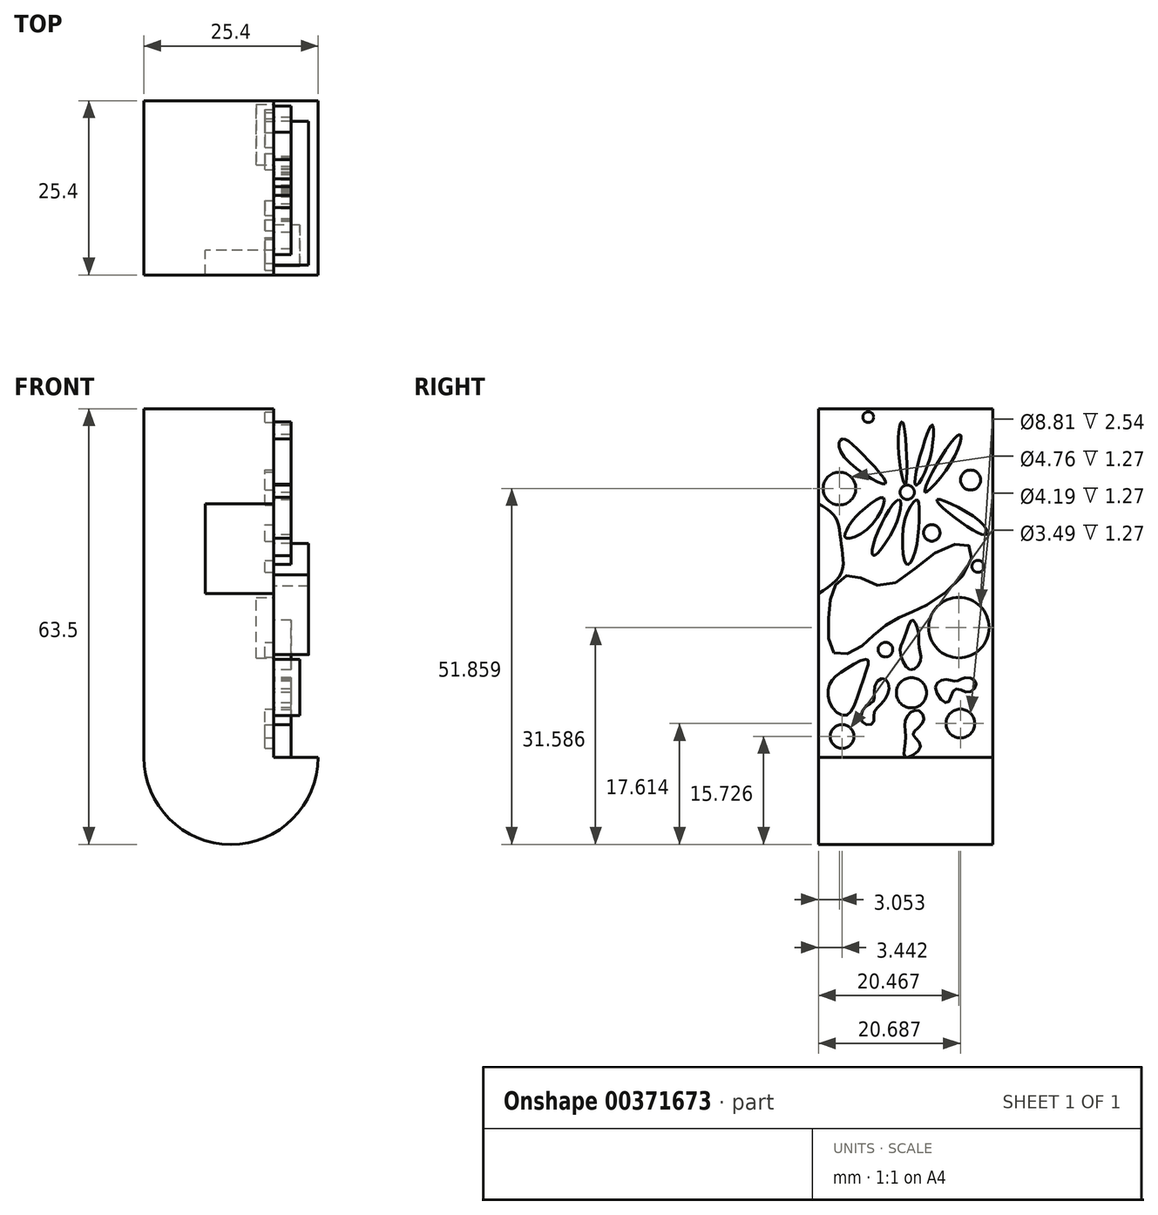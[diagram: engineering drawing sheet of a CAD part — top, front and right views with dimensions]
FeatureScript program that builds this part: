
annotation { "Feature Type Name" : "Feature", "Feature Type Description" : "" }
export const myFeature = defineFeature(function(context is Context, id is Id, definition is map)
    precondition{}
    {
        {
            var Q0;
            Q0=qCreatedBy(makeId("Front.planeOp"),FACE);
            var sketch = newSketch(context, id + "F0", { "sketchPlane" : qUnion([Q0])});
            skLineSegment(sketch, "E0.bottom", {"start": v(0, 0) * mm, "end": v(25.4, 0) * mm});
            skLineSegment(sketch, "E0.top", {"start": v(0, 50.8) * mm, "end": v(25.4, 50.8) * mm});
            skLineSegment(sketch, "E0.left", {"start": v(0, 0) * mm, "end": v(0, 50.8) * mm});
            skArc(sketch, "E1", {"start": v(0, 50.8) * mm, "mid": v(12.7, 63.5) * mm, "end": v(25.4, 50.8) * mm});
            skArc(sketch, "E2", {"start": v(0, 0) * mm, "mid": v(12.7, -12.7) * mm, "end": v(25.4, 0) * mm});
            skLineSegment(sketch, "E3", {"start": v(18.95, 50.8) * mm, "end": v(18.95, 0) * mm});
            skSolve(sketch);
        }
        {
            var Q0;
            {var subQ0=sQuery(id+"F0.wireOp",EDGE,"E0.left");Q0=makeQuery(id+"F0.imprint","IMPRINT",FACE,{"disambiguationData":[TD([[makeQuery(id+"F0.imprint","IMPRINT",EDGE,{"derivedFrom":subQ0}),-1.0]])]});}
            var Q1;
            {var subQ0=sQuery(id+"F0.wireOp",EDGE,"E1");Q1=makeQuery(id+"F0.imprint","IMPRINT",FACE,{"disambiguationData":[TD([[makeQuery(id+"F0.imprint","IMPRINT",EDGE,{"derivedFrom":subQ0}),-1.0]])]});}
            var Q2;
            {var subQ0=sQuery(id+"F0.wireOp",EDGE,"E2");Q2=makeQuery(id+"F0.imprint","IMPRINT",FACE,{"disambiguationData":[TD([[makeQuery(id+"F0.imprint","IMPRINT",EDGE,{"derivedFrom":subQ0}),1.0]])]});}
            extrude(context, id + "F1", {"entities" : qUnion([Q0, Q1, Q2]), "depth" : 25.4 * mm});
        }
        {
            var Q0;
            Q0=makeQuery(id+"F1.opExtrude","SWEPT_FACE",FACE,{"disambiguationData":[OSD([sQuery(id+"F0.wireOp",EDGE,"E3")])]});
            var sketch = newSketch(context, id + "F2", { "sketchPlane" : qUnion([Q0])});
            skPoint(sketch, "E4.5.internal.snap0", {"position": v(-12.7, 0) * mm});
            skPoint(sketch, "E4.6.internal.snap0", {"position": v(-12.7, 0) * mm});
            skFitSpline(sketch, "E4", {"points": [v(-12.7, 0) * mm, v(-10.52, 1.6) * mm, v(-11.6, 3.32) * mm, v(-10.1, 5.28) * mm, v(-11, 6.87) * mm, v(-12.7, 5.47) * mm, v(-12.7, 2.55) * mm, v(-12.7, 0) * mm]});
            skSolve(sketch);
        }
        {
            var Q0;
            Q0 = qSketchRegion(id + "F2", true);
            extrude(context, id + "F3", {"entities" : qUnion([Q0]), "operationType" : NewBodyOperationType.ADD, "depth" : 2.54 * mm});
        }
        {
            var Q0;
            Q0=makeQuery(id+"F1.opExtrude","SWEPT_FACE",FACE,{"disambiguationData":[OSD([sQuery(id+"F0.wireOp",EDGE,"E3")])]});
            var sketch = newSketch(context, id + "F4", { "sketchPlane" : qUnion([Q0])});
            skPoint(sketch, "E5.0.internal.snap0", {"position": v(-19.05, 0) * mm});
            skFitSpline(sketch, "E5", {"points": [v(-19.05, 5.17) * mm, v(-18.56, 7.4) * mm, v(-17.33, 8.22) * mm, v(-17.24, 10.22) * mm, v(-16, 11.47) * mm, v(-15.12, 10.34) * mm, v(-15.97, 8.12) * mm, v(-17.3, 6.48) * mm, v(-17.51, 4.9) * mm, v(-19.05, 5.17) * mm]});
            skSolve(sketch);
        }
        {
            var Q0;
            Q0 = qSketchRegion(id + "F4", true);
            extrude(context, id + "F5", {"entities" : qUnion([Q0]), "operationType" : NewBodyOperationType.ADD, "depth" : 2.54 * mm});
        }
        {
            var Q0;
            Q0=makeQuery(id+"F1.opExtrude","SWEPT_FACE",FACE,{"disambiguationData":[OSD([sQuery(id+"F0.wireOp",EDGE,"E3")])]});
            var sketch = newSketch(context, id + "F6", { "sketchPlane" : qUnion([Q0])});
            skFitSpline(sketch, "E6", {"points": [v(-12.07, 12.76) * mm, v(-10.5, 14.08) * mm, v(-10.77, 16.2) * mm, v(-10.85, 18.32) * mm, v(-11.78, 20) * mm, v(-12.91, 17.3) * mm, v(-13.5, 15.58) * mm, v(-12.07, 12.76) * mm]});
            skSolve(sketch);
        }
        {
            var Q0;
            Q0 = qSketchRegion(id + "F6", true);
            extrude(context, id + "F7", {"entities" : qUnion([Q0]), "operationType" : NewBodyOperationType.ADD, "depth" : 2.54 * mm});
        }
        {
            var Q0;
            Q0=makeQuery(id+"F1.opExtrude","SWEPT_FACE",FACE,{"disambiguationData":[OSD([sQuery(id+"F0.wireOp",EDGE,"E3")])]});
            var sketch = newSketch(context, id + "F8", { "sketchPlane" : qUnion([Q0])});
            skFitSpline(sketch, "E7", {"points": [v(-8.34, 10.18) * mm, v(-6.85, 11.34) * mm, v(-5.38, 11.1) * mm, v(-4.05, 11.6) * mm, v(-2.44, 10.93) * mm, v(-3.5, 9.47) * mm, v(-5.5, 9.91) * mm, v(-6.64, 7.96) * mm, v(-8.34, 10.18) * mm]});
            skSolve(sketch);
        }
        {
            var Q0;
            Q0 = qSketchRegion(id + "F8", true);
            extrude(context, id + "F9", {"entities" : qUnion([Q0]), "operationType" : NewBodyOperationType.ADD, "depth" : 2.54 * mm});
        }
        {
            var Q0;
            Q0=makeQuery(id+"F1.opExtrude","SWEPT_FACE",FACE,{"disambiguationData":[OSD([sQuery(id+"F0.wireOp",EDGE,"E3")])]});
            var sketch = newSketch(context, id + "F10", { "sketchPlane" : qUnion([Q0])});
            skCircle(sketch, "E8", {"center": v(-11.85, 9.4) * mm, "radius": 2.2 * mm});
            skSolve(sketch);
        }
        {
            var Q0;
            Q0 = qSketchRegion(id + "F10", true);
            extrude(context, id + "F11", {"entities" : qUnion([Q0]), "operationType" : NewBodyOperationType.ADD, "depth" : 2.54 * mm});
        }
        {
            var Q0;
            Q0=makeQuery(id+"F1.opExtrude","SWEPT_FACE",FACE,{"disambiguationData":[OSD([sQuery(id+"F0.wireOp",EDGE,"E3")])]});
            var sketch = newSketch(context, id + "F12", { "sketchPlane" : qUnion([Q0])});
            skFitSpline(sketch, "E9", {"points": [v(-13.1, 48.77) * mm, v(-13.77, 46.48) * mm, v(-12.7, 39.85) * mm, v(-13.1, 48.77) * mm]});
            skFitSpline(sketch, "E10", {"points": [v(-11.3, 39.65) * mm, v(-9.84, 46.31) * mm, v(-8.75, 48.41) * mm, v(-9.45, 42.62) * mm, v(-11.3, 39.65) * mm]});
            skFitSpline(sketch, "E11", {"points": [v(-9.88, 38.61) * mm, v(-7.1, 44.43) * mm, v(-4.72, 47.01) * mm, v(-5.78, 43.46) * mm, v(-9.88, 38.61) * mm]});
            skFitSpline(sketch, "E12", {"points": [v(-10.73, 36.42) * mm, v(-11.38, 29.71) * mm, v(-12.51, 28.12) * mm, v(-12.85, 34.44) * mm, v(-11.07, 37.5) * mm, v(-10.73, 36.42) * mm]});
            skFitSpline(sketch, "E13", {"points": [v(-13.72, 37.55) * mm, v(-17.17, 31.81) * mm, v(-17.34, 29.4) * mm, v(-13.82, 34.75) * mm, v(-13.72, 37.55) * mm]});
            skFitSpline(sketch, "E14", {"points": [v(-15.94, 37.84) * mm, v(-19.49, 35.53) * mm, v(-21.08, 33.55) * mm, v(-21.52, 32.03) * mm, v(-17.97, 33.55) * mm, v(-15.94, 37.84) * mm]});
            skFitSpline(sketch, "E15", {"points": [v(-15.65, 39.86) * mm, v(-19.69, 44.89) * mm, v(-22.04, 46.33) * mm, v(-21.98, 44.21) * mm, v(-15.65, 39.86) * mm]});
            skFitSpline(sketch, "E16", {"points": [v(-8.1, 37.57) * mm, v(-1.52, 34.08) * mm, v(-0.95, 32.46) * mm, v(-4.32, 34.02) * mm, v(-8.1, 37.57) * mm]});
            skSolve(sketch);
        }
        {
            var Q0;
            Q0=makeQuery(id+"F12.imprint","IMPRINT",FACE,{"disambiguationData":[TD([[makeQuery(id+"F12.imprint","IMPRINT",EDGE,{"derivedFrom":sQuery(id+"F12.wireOp",EDGE,"E14")}),1.0]])]});
            var Q1;
            Q1=makeQuery(id+"F12.imprint","IMPRINT",FACE,{"disambiguationData":[TD([[makeQuery(id+"F12.imprint","IMPRINT",EDGE,{"derivedFrom":sQuery(id+"F12.wireOp",EDGE,"E15")}),1.0]])]});
            var Q2;
            Q2=makeQuery(id+"F12.imprint","IMPRINT",FACE,{"disambiguationData":[TD([[makeQuery(id+"F12.imprint","IMPRINT",EDGE,{"derivedFrom":sQuery(id+"F12.wireOp",EDGE,"E9")}),1.0]])]});
            var Q3;
            Q3=makeQuery(id+"F12.imprint","IMPRINT",FACE,{"disambiguationData":[TD([[makeQuery(id+"F12.imprint","IMPRINT",EDGE,{"derivedFrom":sQuery(id+"F12.wireOp",EDGE,"E10")}),-1.0]])]});
            var Q4;
            Q4=makeQuery(id+"F12.imprint","IMPRINT",FACE,{"disambiguationData":[TD([[makeQuery(id+"F12.imprint","IMPRINT",EDGE,{"derivedFrom":sQuery(id+"F12.wireOp",EDGE,"E11")}),-1.0]])]});
            var Q5;
            Q5=makeQuery(id+"F12.imprint","IMPRINT",FACE,{"disambiguationData":[TD([[makeQuery(id+"F12.imprint","IMPRINT",EDGE,{"derivedFrom":sQuery(id+"F12.wireOp",EDGE,"E16")}),-1.0]])]});
            var Q6;
            Q6=makeQuery(id+"F12.imprint","IMPRINT",FACE,{"disambiguationData":[TD([[makeQuery(id+"F12.imprint","IMPRINT",EDGE,{"derivedFrom":sQuery(id+"F12.wireOp",EDGE,"E12")}),-1.0]])]});
            var Q7;
            Q7=makeQuery(id+"F12.imprint","IMPRINT",FACE,{"disambiguationData":[TD([[makeQuery(id+"F12.imprint","IMPRINT",EDGE,{"derivedFrom":sQuery(id+"F12.wireOp",EDGE,"E13")}),1.0]])]});
            extrude(context, id + "F13", {"entities" : qUnion([Q0, Q1, Q2, Q3, Q4, Q5, Q6, Q7]), "operationType" : NewBodyOperationType.ADD, "depth" : 2.54 * mm});
        }
        {
            var Q0;
            Q0=makeQuery(id+"F1.opExtrude","SWEPT_FACE",FACE,{"disambiguationData":[OSD([sQuery(id+"F0.wireOp",EDGE,"E3")])]});
            var sketch = newSketch(context, id + "F14", { "sketchPlane" : qUnion([Q0])});
            skCircle(sketch, "E17", {"center": v(-12.47, 38.61) * mm, "radius": 1.05 * mm});
            skSolve(sketch);
        }
        {
            var Q0;
            Q0 = qSketchRegion(id + "F14", true);
            extrude(context, id + "F15", {"entities" : qUnion([Q0]), "operationType" : NewBodyOperationType.ADD, "depth" : 2.54 * mm});
        }
        {
            var Q0;
            Q0=makeQuery(id+"F1.opExtrude","SWEPT_FACE",FACE,{"disambiguationData":[OSD([sQuery(id+"F0.wireOp",EDGE,"E3")])]});
            var sketch = newSketch(context, id + "F16", { "sketchPlane" : qUnion([Q0])});
            skCircle(sketch, "E18", {"center": v(-4.93, 18.89) * mm, "radius": 4.4 * mm});
            skSolve(sketch);
        }
        {
            var Q0;
            Q0 = qSketchRegion(id + "F16", true);
            extrude(context, id + "F17", {"entities" : qUnion([Q0]), "operationType" : NewBodyOperationType.REMOVE, "oppositeDirection" : true, "depth" : 2.54 * mm});
        }
        {
            var Q0;
            Q0=makeQuery(id+"F1.opExtrude","SWEPT_FACE",FACE,{"disambiguationData":[OSD([sQuery(id+"F0.wireOp",EDGE,"E3")])]});
            var sketch = newSketch(context, id + "F18", { "sketchPlane" : qUnion([Q0])});
            skFitSpline(sketch, "E19", {"points": [v(-23.17, 15.24) * mm, v(-19.76, 15.76) * mm, v(-16.74, 18.38) * mm, v(-13.33, 20.52) * mm, v(-9.96, 22.02) * mm, v(-3.7, 27.44) * mm, v(-3.48, 30.83) * mm, v(-8.37, 29.8) * mm, v(-15.73, 24.96) * mm, v(-20.42, 26.56) * mm, v(-23.05, 24.96) * mm, v(-23.93, 20.13) * mm, v(-23.17, 15.24) * mm]});
            skSolve(sketch);
        }
        {
            var Q0;
            Q0 = qSketchRegion(id + "F18", true);
            extrude(context, id + "F19", {"entities" : qUnion([Q0]), "operationType" : NewBodyOperationType.ADD, "depth" : 5.08 * mm});
        }
        {
            var Q0;
            Q0=makeQuery(id+"F1.opExtrude","SWEPT_FACE",FACE,{"disambiguationData":[OSD([sQuery(id+"F0.wireOp",EDGE,"E3")])]});
            var sketch = newSketch(context, id + "F20", { "sketchPlane" : qUnion([Q0])});
            skFitSpline(sketch, "E20", {"points": [v(-23.83, 10.6) * mm, v(-21.7, 12.63) * mm, v(-18.28, 14.25) * mm, v(-18.98, 11.06) * mm, v(-21.29, 6.12) * mm, v(-23.55, 7.55) * mm, v(-23.83, 10.6) * mm]});
            skSolve(sketch);
        }
        {
            var Q0;
            Q0 = qSketchRegion(id + "F20", true);
            extrude(context, id + "F21", {"entities" : qUnion([Q0]), "operationType" : NewBodyOperationType.ADD, "depth" : 3.8 * mm});
        }
        {
            var Q0;
            Q0=makeQuery(id+"F1.opExtrude","SWEPT_FACE",FACE,{"disambiguationData":[OSD([sQuery(id+"F0.wireOp",EDGE,"E3")])]});
            var sketch = newSketch(context, id + "F22", { "sketchPlane" : qUnion([Q0])});
            skCircle(sketch, "E21", {"center": v(-3.23, 40.4) * mm, "radius": 1.46 * mm});
            skCircle(sketch, "E22", {"center": v(-2.16, 27.82) * mm, "radius": 0.88 * mm});
            skCircle(sketch, "E23", {"center": v(-8.88, 32.7) * mm, "radius": 1.2 * mm});
            skCircle(sketch, "E24", {"center": v(-22.35, 39.16) * mm, "radius": 2.38 * mm});
            skCircle(sketch, "E25", {"center": v(-18.14, 49.57) * mm, "radius": 0.78 * mm});
            skCircle(sketch, "E26", {"center": v(-15.64, 15.68) * mm, "radius": 1.07 * mm});
            skCircle(sketch, "E27", {"center": v(-4.71, 4.91) * mm, "radius": 2.1 * mm});
            skCircle(sketch, "E28", {"center": v(-21.96, 3.03) * mm, "radius": 1.74 * mm});
            skSolve(sketch);
        }
        {
            var Q0;
            Q0 = qSketchRegion(id + "F22", true);
            extrude(context, id + "F23", {"entities" : qUnion([Q0]), "operationType" : NewBodyOperationType.REMOVE, "oppositeDirection" : true, "depth" : 1.27 * mm});
        }
        {
            var Q0;
            Q0=makeQuery(id+"F1.opExtrude","SWEPT_FACE",FACE,{"disambiguationData":[OSD([sQuery(id+"F0.wireOp",EDGE,"E3")])]});
            var sketch = newSketch(context, id + "F24", { "sketchPlane" : qUnion([Q0])});
            skFitSpline(sketch, "E29", {"points": [v(-25.4, 36.94) * mm, v(-22.84, 34.8) * mm, v(-22.1, 31.15) * mm, v(-22.03, 26.97) * mm, v(-25.4, 23.87) * mm], "startDerivative": vector(13.25, -7.95) * mm, "endDerivative": vector(-15.98, -10.25) * mm});
            skSolve(sketch);
        }
        {
            var Q0;
            {var subQ0=sQuery(id+"F24.wireOp",EDGE,"E29");Q0=makeQuery(id+"F24.imprint","IMPRINT",FACE,{"disambiguationData":[TD([[makeQuery(id+"F24.imprint","IMPRINT",EDGE,{"derivedFrom":subQ0}),-1.0]])]});}
            extrude(context, id + "F25", {"entities" : qUnion([Q0]), "operationType" : NewBodyOperationType.REMOVE, "oppositeDirection" : true, "depth" : 10 * mm});
        }
        {
            var Q0;
            Q0=qCreatedBy(makeId("Right.planeOp"),FACE);
            var sketch = newSketch(context, id + "F26", { "sketchPlane" : qUnion([Q0])});
            skCircle(sketch, "E30", {"center": v(-12.67, 58.1) * mm, "radius": 4.19 * mm});
            skSolve(sketch);
        }
        {
            var Q0;
            Q0 = qSketchRegion(id + "F26", true);
            extrude(context, id + "F27", {"entities" : qUnion([Q0]), "operationType" : NewBodyOperationType.REMOVE, "oppositeDirection" : true, "depth" : 30 * mm});
        }
        {
            var Q0;
            Q0=qCreatedBy(makeId("Right.planeOp"),FACE);
            var sketch = newSketch(context, id + "F28", { "sketchPlane" : qUnion([Q0])});
            skCircle(sketch, "E31", {"center": v(-13.1, 57.93) * mm, "radius": 4.37 * mm});
            skSolve(sketch);
        }
        {
            var Q0;
            Q0 = qSketchRegion(id + "F28", true);
            extrude(context, id + "F29", {"entities" : qUnion([Q0]), "operationType" : NewBodyOperationType.REMOVE, "depth" : 30 * mm});
        }
    });
